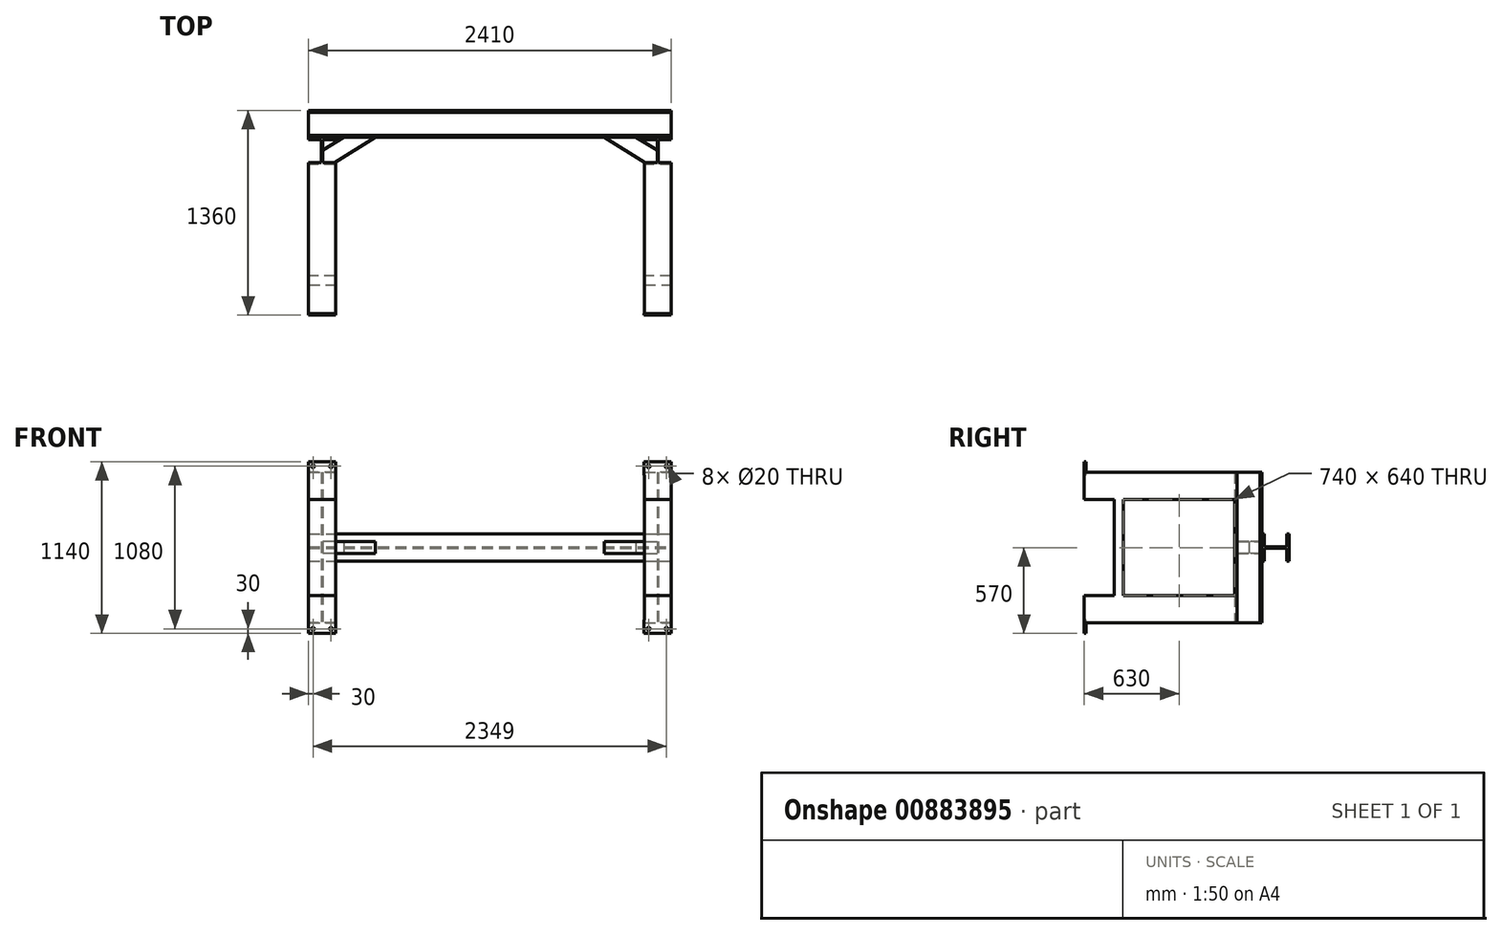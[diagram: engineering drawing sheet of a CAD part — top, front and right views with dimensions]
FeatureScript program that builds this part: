
annotation { "Feature Type Name" : "Feature", "Feature Type Description" : "" }
export const myFeature = defineFeature(function(context is Context, id is Id, definition is map)
    precondition{}
    {
        {
            var Q0;
            Q0=qCreatedBy(makeId("Top.planeOp"),FACE);
            var sketch = newSketch(context, id + "F0", { "sketchPlane" : qUnion([Q0])});
            skLineSegment(sketch, "E0.bottom", {"start": v(-1024.5, -90) * mm, "end": v(-1204.5, -90) * mm});
            skLineSegment(sketch, "E0.top", {"start": v(-1024.5, 90) * mm, "end": v(-1204.5, 90) * mm});
            skLineSegment(sketch, "E0.left", {"start": v(-1024.5, -90) * mm, "end": v(-1024.5, -76) * mm});
            skLineSegment(sketch, "E0.right", {"start": v(-1204.5, -90) * mm, "end": v(-1204.5, -76) * mm});
            skPoint(sketch, "E0.middle", {"position": v(-1114.5, 0) * mm});
            skLineSegment(sketch, "E1.bottom", {"start": v(-1204.5, 76) * mm, "end": v(-1110.25, 76) * mm});
            skLineSegment(sketch, "E1.top", {"start": v(-1204.5, -76) * mm, "end": v(-1110.25, -76) * mm});
            skLineSegment(sketch, "E1.right", {"start": v(-1110.25, 76) * mm, "end": v(-1110.25, -76) * mm});
            skLineSegment(sketch, "E2.bottom", {"start": v(-1024.5, 76) * mm, "end": v(-1118.75, 76) * mm});
            skLineSegment(sketch, "E2.top", {"start": v(-1024.5, -76) * mm, "end": v(-1118.75, -76) * mm});
            skLineSegment(sketch, "E2.right", {"start": v(-1118.75, 76) * mm, "end": v(-1118.75, -76) * mm});
            skLineSegment(sketch, "E3.trimOffspring", {"start": v(-1024.5, 76) * mm, "end": v(-1024.5, 90) * mm});
            skLineSegment(sketch, "E4.trimOffspring", {"start": v(-1204.5, 76) * mm, "end": v(-1204.5, 90) * mm});
            skLineSegment(sketch, "E5.MirrorCS", {"start": v(1204.5, -90) * mm, "end": v(1204.5, -76) * mm});
            skLineSegment(sketch, "E6.MirrorCS", {"start": v(1024.5, 76) * mm, "end": v(1024.5, 90) * mm});
            skLineSegment(sketch, "E7.MirrorCS", {"start": v(1024.5, -90) * mm, "end": v(1024.5, -76) * mm});
            skLineSegment(sketch, "E8.MirrorCS", {"start": v(1204.5, 76) * mm, "end": v(1204.5, 90) * mm});
            skLineSegment(sketch, "E9.MirrorCS", {"start": v(1024.5, -90) * mm, "end": v(1204.5, -90) * mm});
            skLineSegment(sketch, "E10.MirrorCS", {"start": v(1024.5, -76) * mm, "end": v(1118.75, -76) * mm});
            skLineSegment(sketch, "E11.MirrorCS", {"start": v(1204.5, 76) * mm, "end": v(1110.25, 76) * mm});
            skPoint(sketch, "E12.MirrorP", {"position": v(1114.5, 0) * mm});
            skLineSegment(sketch, "E13.MirrorCS", {"start": v(1110.25, 76) * mm, "end": v(1110.25, -76) * mm});
            skLineSegment(sketch, "E14.MirrorCS", {"start": v(1024.5, 76) * mm, "end": v(1118.75, 76) * mm});
            skLineSegment(sketch, "E15.MirrorCS", {"start": v(1024.5, 90) * mm, "end": v(1204.5, 90) * mm});
            skLineSegment(sketch, "E16.MirrorCS", {"start": v(1118.75, 76) * mm, "end": v(1118.75, -76) * mm});
            skLineSegment(sketch, "E17.MirrorCS", {"start": v(1204.5, -76) * mm, "end": v(1110.25, -76) * mm});
            skSolve(sketch);
        }
        {
            var Q0;
            Q0 = qSketchRegion(id + "F0", true);
            extrude(context, id + "F1", {"entities" : qUnion([Q0]), "endBound" : BoundingType.SYMMETRIC, "depth" : 1000 * mm, "offsetDistance" : 25 * mm});
        }
        {
            var Q0;
            Q0=makeQuery(id+"F1.opExtrude","SWEPT_FACE",FACE,{"disambiguationData":[OSD([sQuery(id+"F0.wireOp",EDGE,"E8.MirrorCS")])]});
            var sketch = newSketch(context, id + "F2", { "sketchPlane" : qUnion([Q0])});
            skLineSegment(sketch, "E18.bottom", {"start": v(90, -90) * mm, "end": v(104, -90) * mm});
            skLineSegment(sketch, "E18.top", {"start": v(90, 90) * mm, "end": v(104, 90) * mm});
            skLineSegment(sketch, "E18.left", {"start": v(90, -90) * mm, "end": v(90, 90) * mm});
            skLineSegment(sketch, "E18.right", {"start": v(270, -90) * mm, "end": v(270, 90) * mm});
            skPoint(sketch, "E18.middle", {"position": v(180, 0) * mm});
            skLineSegment(sketch, "E19.top", {"start": v(256, 4.25) * mm, "end": v(104, 4.25) * mm});
            skLineSegment(sketch, "E19.left", {"start": v(256, 90) * mm, "end": v(256, 4.25) * mm});
            skLineSegment(sketch, "E19.right", {"start": v(104, 90) * mm, "end": v(104, 4.25) * mm});
            skLineSegment(sketch, "E20.top", {"start": v(256, -4.25) * mm, "end": v(104, -4.25) * mm});
            skLineSegment(sketch, "E20.left", {"start": v(256, -90) * mm, "end": v(256, -4.25) * mm});
            skLineSegment(sketch, "E20.right", {"start": v(104, -90) * mm, "end": v(104, -4.25) * mm});
            skLineSegment(sketch, "E21.trimOffspring", {"start": v(256, 90) * mm, "end": v(270, 90) * mm});
            skLineSegment(sketch, "E22.trimOffspring", {"start": v(256, -90) * mm, "end": v(270, -90) * mm});
            skSolve(sketch);
        }
        {
            var Q0;
            Q0 = qSketchRegion(id + "F2", true);
            extrude(context, id + "F3", {"entities" : qUnion([Q0]), "oppositeDirection" : true, "depth" : 2409 * mm, "offsetDistance" : 25 * mm});
        }
        {
            var Q0;
            Q0=makeQuery(id+"F1.opExtrude","SWEPT_FACE",FACE,{"disambiguationData":[OSD([sQuery(id+"F0.wireOp",EDGE,"E9.MirrorCS")])]});
            var sketch = newSketch(context, id + "F4", { "sketchPlane" : qUnion([Q0])});
            skLineSegment(sketch, "E23.bottom", {"start": v(1204.5, -500) * mm, "end": v(1024.5, -500) * mm});
            skLineSegment(sketch, "E23.top", {"start": v(1204.5, -320) * mm, "end": v(1024.5, -320) * mm});
            skLineSegment(sketch, "E23.left", {"start": v(1204.5, -500) * mm, "end": v(1204.5, -320) * mm});
            skLineSegment(sketch, "E23.right", {"start": v(1024.5, -500) * mm, "end": v(1024.5, -320) * mm});
            skLineSegment(sketch, "E24.0.1.0", {"start": v(1204.5, 500) * mm, "end": v(1024.5, 500) * mm});
            skLineSegment(sketch, "E24.0.1.1", {"start": v(1024.5, 320) * mm, "end": v(1024.5, 500) * mm});
            skLineSegment(sketch, "E24.0.1.2", {"start": v(1204.5, 320) * mm, "end": v(1024.5, 320) * mm});
            skLineSegment(sketch, "E24.0.1.3", {"start": v(1204.5, 320) * mm, "end": v(1204.5, 500) * mm});
            skLineSegment(sketch, "E24.1.0.0", {"start": v(-1025.5, -320) * mm, "end": v(-1205.5, -320) * mm});
            skLineSegment(sketch, "E24.1.0.1", {"start": v(-1205.5, -500) * mm, "end": v(-1205.5, -320) * mm});
            skLineSegment(sketch, "E24.1.0.2", {"start": v(-1025.5, -500) * mm, "end": v(-1205.5, -500) * mm});
            skLineSegment(sketch, "E24.1.0.3", {"start": v(-1025.5, -500) * mm, "end": v(-1025.5, -320) * mm});
            skLineSegment(sketch, "E24.1.1.0", {"start": v(-1025.5, 500) * mm, "end": v(-1205.5, 500) * mm});
            skLineSegment(sketch, "E24.1.1.1", {"start": v(-1205.5, 320) * mm, "end": v(-1205.5, 500) * mm});
            skLineSegment(sketch, "E24.1.1.2", {"start": v(-1025.5, 320) * mm, "end": v(-1205.5, 320) * mm});
            skLineSegment(sketch, "E24.1.1.3", {"start": v(-1025.5, 320) * mm, "end": v(-1025.5, 500) * mm});
            skLineSegment(sketch, "E24.direction1", {"start": v(1024.5, -500) * mm, "end": v(-1205.5, -500) * mm, "construction": true});
            skLineSegment(sketch, "E24.direction2", {"start": v(1024.5, -500) * mm, "end": v(1024.5, 320) * mm, "construction": true});
            skSolve(sketch);
        }
        {
            var Q0;
            Q0=makeQuery(id+"F4.imprint","IMPRINT",FACE,{"disambiguationData":[TD([[makeQuery(id+"F4.imprint","IMPRINT",EDGE,{"derivedFrom":sQuery(id+"F4.wireOp",EDGE,"E23.bottom")}),1.0]])]});
            var Q1;
            Q1=makeQuery(id+"F4.imprint","IMPRINT",FACE,{"disambiguationData":[TD([[makeQuery(id+"F4.imprint","IMPRINT",EDGE,{"derivedFrom":sQuery(id+"F4.wireOp",EDGE,"E24.1.0.0")}),1.0]])]});
            var Q2;
            Q2=makeQuery(id+"F4.imprint","IMPRINT",FACE,{"disambiguationData":[TD([[makeQuery(id+"F4.imprint","IMPRINT",EDGE,{"derivedFrom":sQuery(id+"F4.wireOp",EDGE,"E24.1.1.0")}),1.0]])]});
            var Q3;
            Q3=makeQuery(id+"F4.imprint","IMPRINT",FACE,{"disambiguationData":[TD([[makeQuery(id+"F4.imprint","IMPRINT",EDGE,{"derivedFrom":sQuery(id+"F4.wireOp",EDGE,"E24.0.1.0")}),-1.0]])]});
            extrude(context, id + "F5", {"entities" : qUnion([Q0, Q1, Q2, Q3]), "operationType" : NewBodyOperationType.ADD, "depth" : 1000 * mm, "offsetDistance" : 25 * mm});
        }
        {
            var Q0;
            Q0=makeQuery(id+"F5.opExtrude","SWEPT_FACE",FACE,{"disambiguationData":[OSD([sQuery(id+"F4.wireOp",EDGE,"E24.0.1.2")])]});
            var sketch = newSketch(context, id + "F6", { "sketchPlane" : qUnion([Q0])});
            skLineSegment(sketch, "E25.bottom", {"start": v(1024.5, 830) * mm, "end": v(1204.5, 830) * mm});
            skLineSegment(sketch, "E25.top", {"start": v(1024.5, 890) * mm, "end": v(1204.5, 890) * mm});
            skLineSegment(sketch, "E25.left", {"start": v(1024.5, 830) * mm, "end": v(1024.5, 890) * mm});
            skLineSegment(sketch, "E25.right", {"start": v(1204.5, 830) * mm, "end": v(1204.5, 890) * mm});
            skSolve(sketch);
        }
        {
            var Q0;
            Q0=makeQuery(id+"F6.imprint","IMPRINT",FACE,{"disambiguationData":[TD([[makeQuery(id+"F6.imprint","IMPRINT",EDGE,{"derivedFrom":sQuery(id+"F6.wireOp",EDGE,"E25.bottom")}),1.0]])]});
            extrude(context, id + "F7", {"entities" : qUnion([Q0]), "operationType" : NewBodyOperationType.ADD, "depth" : 700 * mm, "offsetDistance" : 25 * mm});
        }
        {
            var Q0;
            Q0=makeQuery(id+"F5.opExtrude","SWEPT_FACE",FACE,{"disambiguationData":[OSD([sQuery(id+"F4.wireOp",EDGE,"E24.1.1.2")])]});
            var sketch = newSketch(context, id + "F8", { "sketchPlane" : qUnion([Q0])});
            skLineSegment(sketch, "E26.bottom", {"start": v(-1205.5, 830) * mm, "end": v(-1025.5, 830) * mm});
            skLineSegment(sketch, "E26.top", {"start": v(-1205.5, 890) * mm, "end": v(-1025.5, 890) * mm});
            skLineSegment(sketch, "E26.left", {"start": v(-1205.5, 830) * mm, "end": v(-1205.5, 890) * mm});
            skLineSegment(sketch, "E26.right", {"start": v(-1025.5, 830) * mm, "end": v(-1025.5, 890) * mm});
            skSolve(sketch);
        }
        {
            var Q0;
            Q0=makeQuery(id+"F8.imprint","IMPRINT",FACE,{"disambiguationData":[TD([[makeQuery(id+"F8.imprint","IMPRINT",EDGE,{"derivedFrom":sQuery(id+"F8.wireOp",EDGE,"E26.bottom")}),1.0]])]});
            extrude(context, id + "F9", {"entities" : qUnion([Q0]), "operationType" : NewBodyOperationType.ADD, "depth" : 700 * mm, "offsetDistance" : 25 * mm});
        }
        {
            var Q0;
            Q0=qCreatedBy(makeId("Top.planeOp"),FACE);
            var sketch = newSketch(context, id + "F10", { "sketchPlane" : qUnion([Q0])});
            skLineSegment(sketch, "E27.0", {"start": v(-970.25, 90) * mm, "end": v(-760.02, 90) * mm});
            skLineSegment(sketch, "E28.0", {"start": v(-1110.25, 4) * mm, "end": v(-1110.25, -76) * mm});
            skLineSegment(sketch, "E29.0", {"start": v(-1030.25, -76) * mm, "end": v(-1110.25, -76) * mm});
            skLineSegment(sketch, "E30.bottom", {"start": v(-1110.25, -76) * mm, "end": v(-1030.25, -76) * mm});
            skLineSegment(sketch, "E30.left", {"start": v(-1110.25, -76) * mm, "end": v(-1110.25, 4) * mm});
            skLineSegment(sketch, "E31.bottom", {"start": v(-970.25, 90) * mm, "end": v(-890.25, 90) * mm});
            skLineSegment(sketch, "E32", {"start": v(-970.25, 90) * mm, "end": v(-1110.25, 4) * mm});
            skLineSegment(sketch, "E33", {"start": v(-1030.25, -76) * mm, "end": v(-890.25, 10) * mm});
            skLineSegment(sketch, "E34", {"start": v(-890.25, 10) * mm, "end": v(-760.02, 90) * mm});
            skPoint(sketch, "E35.orphan", {"position": v(-1204.5, 90) * mm});
            skPoint(sketch, "E36.orphan", {"position": v(-1110.25, 76) * mm});
            skPoint(sketch, "E37.orphan", {"position": v(1204.5, 90) * mm});
            skPoint(sketch, "E38.orphan", {"position": v(-1024.5, -76) * mm});
            skLineSegment(sketch, "E39.MirrorCS", {"start": v(1110.25, 4) * mm, "end": v(1110.25, -76) * mm});
            skLineSegment(sketch, "E40.MirrorCS", {"start": v(1030.25, -76) * mm, "end": v(1110.25, -76) * mm});
            skPoint(sketch, "E41.MirrorP", {"position": v(1024.5, -76) * mm});
            skPoint(sketch, "E42.MirrorP", {"position": v(1110.25, 76) * mm});
            skLineSegment(sketch, "E43.MirrorCS", {"start": v(970.25, 90) * mm, "end": v(1110.25, 4) * mm});
            skLineSegment(sketch, "E44.MirrorCS", {"start": v(1030.25, -76) * mm, "end": v(890.25, 10) * mm});
            skLineSegment(sketch, "E45.MirrorCS", {"start": v(970.25, 90) * mm, "end": v(890.25, 90) * mm});
            skLineSegment(sketch, "E46.MirrorCS", {"start": v(890.25, 10) * mm, "end": v(760.02, 90) * mm});
            skLineSegment(sketch, "E47.MirrorCS", {"start": v(1110.25, -76) * mm, "end": v(1030.25, -76) * mm});
            skLineSegment(sketch, "E48.MirrorCS", {"start": v(970.25, 90) * mm, "end": v(760.02, 90) * mm});
            skLineSegment(sketch, "E49.MirrorCS", {"start": v(1110.25, -76) * mm, "end": v(1110.25, 4) * mm});
            skSolve(sketch);
        }
        {
            var Q0;
            Q0=makeQuery(id+"F10.imprint","IMPRINT",FACE,{"disambiguationData":[TD([[makeQuery(id+"F10.imprint","IMPRINT",EDGE,{"derivedFrom":sQuery(id+"F10.wireOp",EDGE,"E27.0")}),-1.0]])]});
            var Q1;
            {var subQ1=sQuery(id+"F10.wireOp",EDGE,"E43.MirrorCS");Q1=makeQuery(id+"F10.imprint","IMPRINT",FACE,{"disambiguationData":[TD([[makeQuery(id+"F10.imprint","IMPRINT",EDGE,{"derivedFrom":subQ1}),-1.0]])]});}
            extrude(context, id + "F11", {"entities" : qUnion([Q0, Q1]), "endBound" : BoundingType.SYMMETRIC, "depth" : 80 * mm, "offsetDistance" : 25 * mm});
        }
        {
            var Q0;
            Q0=makeQuery(id+"F5.opExtrude","CAP_FACE",FACE,{"disambiguationData":[OSD([sQuery(id+"F4.wireOp",EDGE,"E24.1.1.0"),sQuery(id+"F4.wireOp",EDGE,"E24.1.1.1"),sQuery(id+"F4.wireOp",EDGE,"E24.1.1.2"),sQuery(id+"F4.wireOp",EDGE,"E24.1.1.3")])],"isStart":false});
            var sketch = newSketch(context, id + "F12", { "sketchPlane" : qUnion([Q0])});
            skLineSegment(sketch, "E50.bottom", {"start": v(-1205.5, 480) * mm, "end": v(-1025.5, 480) * mm});
            skLineSegment(sketch, "E50.top", {"start": v(-1205.5, 570) * mm, "end": v(-1025.5, 570) * mm});
            skLineSegment(sketch, "E50.left", {"start": v(-1205.5, 480) * mm, "end": v(-1205.5, 570) * mm});
            skLineSegment(sketch, "E50.right", {"start": v(-1025.5, 480) * mm, "end": v(-1025.5, 570) * mm});
            skLineSegment(sketch, "E51.0.1.0", {"start": v(-1205.5, -570) * mm, "end": v(-1025.5, -570) * mm});
            skLineSegment(sketch, "E51.0.1.1", {"start": v(-1205.5, -480) * mm, "end": v(-1025.5, -480) * mm});
            skLineSegment(sketch, "E51.0.1.2", {"start": v(-1025.5, -570) * mm, "end": v(-1025.5, -480) * mm});
            skLineSegment(sketch, "E51.0.1.3", {"start": v(-1205.5, -570) * mm, "end": v(-1205.5, -480) * mm});
            skLineSegment(sketch, "E51.1.0.0", {"start": v(1023.5, 480) * mm, "end": v(1203.5, 480) * mm});
            skLineSegment(sketch, "E51.1.0.1", {"start": v(1023.5, 570) * mm, "end": v(1203.5, 570) * mm});
            skLineSegment(sketch, "E51.1.0.2", {"start": v(1203.5, 480) * mm, "end": v(1203.5, 570) * mm});
            skLineSegment(sketch, "E51.1.0.3", {"start": v(1023.5, 480) * mm, "end": v(1023.5, 570) * mm});
            skLineSegment(sketch, "E51.1.1.0", {"start": v(1023.5, -570) * mm, "end": v(1203.5, -570) * mm});
            skLineSegment(sketch, "E51.1.1.1", {"start": v(1023.5, -480) * mm, "end": v(1203.5, -480) * mm});
            skLineSegment(sketch, "E51.1.1.2", {"start": v(1203.5, -570) * mm, "end": v(1203.5, -480) * mm});
            skLineSegment(sketch, "E51.1.1.3", {"start": v(1023.5, -570) * mm, "end": v(1023.5, -480) * mm});
            skLineSegment(sketch, "E51.direction1", {"start": v(-1205.5, 480) * mm, "end": v(1023.5, 480) * mm, "construction": true});
            skLineSegment(sketch, "E51.direction2", {"start": v(-1205.5, 480) * mm, "end": v(-1205.5, -570) * mm, "construction": true});
            skSolve(sketch);
        }
        {
            var Q0;
            Q0 = qSketchRegion(id + "F12", true);
            extrude(context, id + "F13", {"entities" : qUnion([Q0]), "operationType" : NewBodyOperationType.ADD, "oppositeDirection" : true, "depth" : 10 * mm, "offsetDistance" : 25 * mm});
        }
        {
            var Q0;
            Q0=makeQuery(id+"F13.boolean.opBoolean","MERGE",FACE,{"derivedFrom":[makeQuery(id+"F5.opExtrude","CAP_FACE",FACE,{"disambiguationData":[OSD([sQuery(id+"F4.wireOp",EDGE,"E24.1.1.0"),sQuery(id+"F4.wireOp",EDGE,"E24.1.1.1"),sQuery(id+"F4.wireOp",EDGE,"E24.1.1.2"),sQuery(id+"F4.wireOp",EDGE,"E24.1.1.3")])],"isStart":false}),makeQuery(id+"F13.opExtrude","CAP_FACE",FACE,{"disambiguationData":[OSD([sQuery(id+"F12.wireOp",EDGE,"E50.bottom"),sQuery(id+"F12.wireOp",EDGE,"E50.top"),sQuery(id+"F12.wireOp",EDGE,"E50.left"),sQuery(id+"F12.wireOp",EDGE,"E50.right")])],"isStart":true})]});
            var sketch = newSketch(context, id + "F14", { "sketchPlane" : qUnion([Q0])});
            skCircle(sketch, "E52", {"center": v(-1175.5, 540) * mm, "radius": 10 * mm});
            skCircle(sketch, "E53", {"center": v(-1055.5, 540) * mm, "radius": 10 * mm});
            skCircle(sketch, "E54.0.1.0", {"center": v(-1055.5, -540) * mm, "radius": 10 * mm});
            skCircle(sketch, "E54.0.1.1", {"center": v(-1175.5, -540) * mm, "radius": 10 * mm});
            skCircle(sketch, "E54.1.0.0", {"center": v(1173.5, 540) * mm, "radius": 10 * mm});
            skCircle(sketch, "E54.1.0.1", {"center": v(1053.5, 540) * mm, "radius": 10 * mm});
            skCircle(sketch, "E54.1.1.0", {"center": v(1173.5, -540) * mm, "radius": 10 * mm});
            skCircle(sketch, "E54.1.1.1", {"center": v(1053.5, -540) * mm, "radius": 10 * mm});
            skLineSegment(sketch, "E54.direction1", {"start": v(-1175.5, 540) * mm, "end": v(1053.5, 540) * mm, "construction": true});
            skLineSegment(sketch, "E54.direction2", {"start": v(-1175.5, 540) * mm, "end": v(-1175.5, -540) * mm, "construction": true});
            skSolve(sketch);
        }
        {
            var Q0;
            Q0 = qSketchRegion(id + "F14", true);
            extrude(context, id + "F15", {"entities" : qUnion([Q0]), "operationType" : NewBodyOperationType.REMOVE, "oppositeDirection" : true, "depth" : 25 * mm, "offsetDistance" : 25 * mm});
        }
    });
